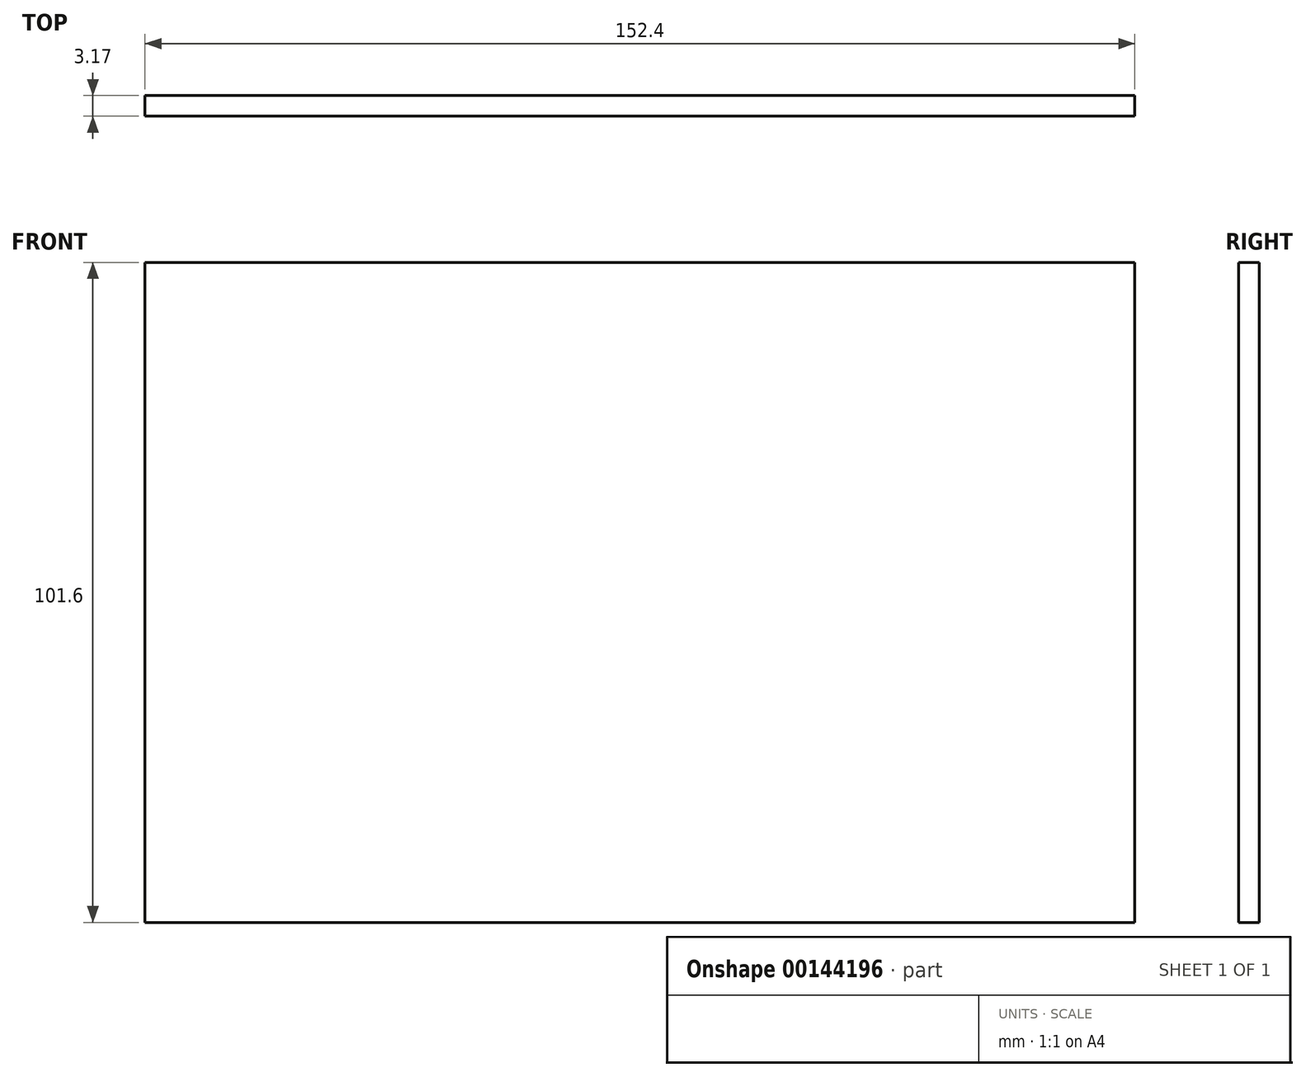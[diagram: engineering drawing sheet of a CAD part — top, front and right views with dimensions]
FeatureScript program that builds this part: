
annotation { "Feature Type Name" : "Feature", "Feature Type Description" : "" }
export const myFeature = defineFeature(function(context is Context, id is Id, definition is map)
    precondition{}
    {
        {
            var Q0;
            Q0=qCreatedBy(makeId("Front.planeOp"),FACE);
            var sketch = newSketch(context, id + "F0", { "sketchPlane" : qUnion([Q0])});
            skLineSegment(sketch, "E0.bottom", {"start": v(-76.82, 53.16) * mm, "end": v(75.58, 53.16) * mm});
            skLineSegment(sketch, "E0.top", {"start": v(-76.82, -48.44) * mm, "end": v(75.58, -48.44) * mm});
            skLineSegment(sketch, "E0.left", {"start": v(-76.82, 53.16) * mm, "end": v(-76.82, -48.44) * mm});
            skLineSegment(sketch, "E0.right", {"start": v(75.58, 53.16) * mm, "end": v(75.58, -48.44) * mm});
            skSolve(sketch);
        }
        {
            var Q0;
            Q0 = qSketchRegion(id + "F0", true);
            extrude(context, id + "F1", {"entities" : qUnion([Q0]), "depth" : 3.17 * mm});
        }
    });
